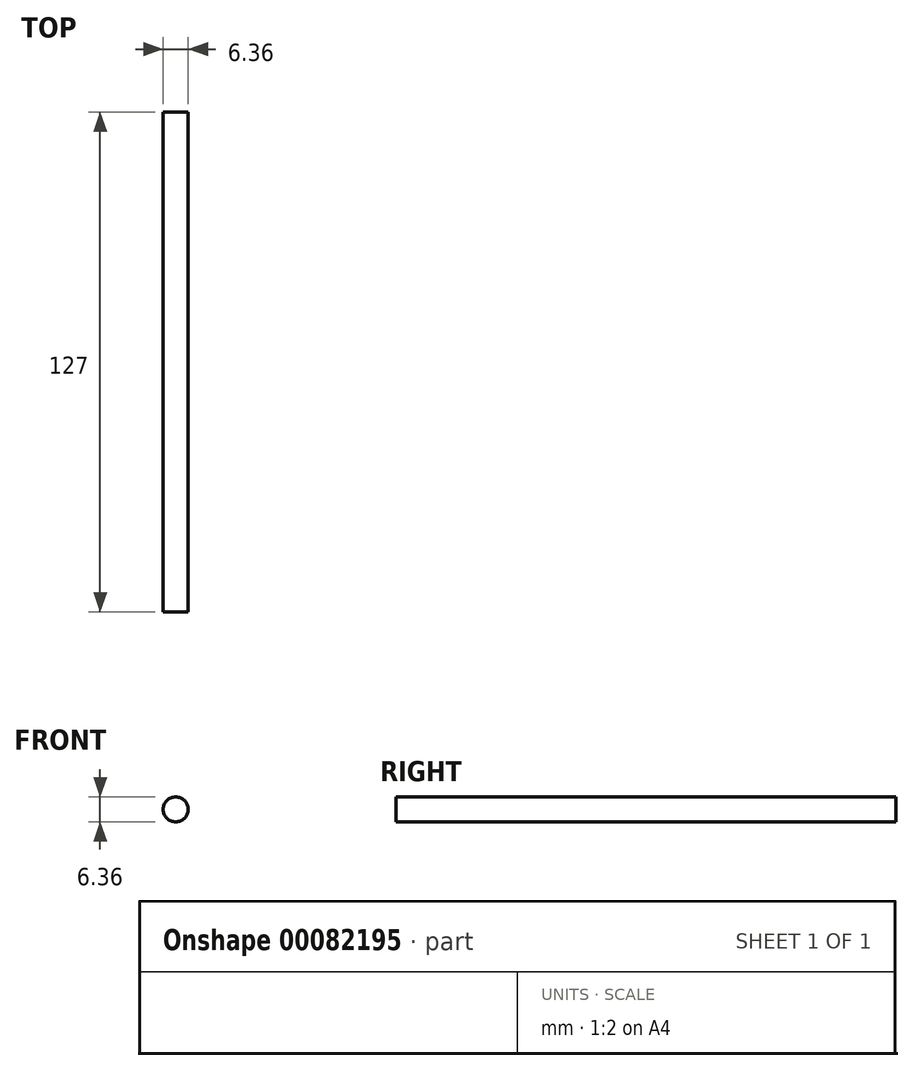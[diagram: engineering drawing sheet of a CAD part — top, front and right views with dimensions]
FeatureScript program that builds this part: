
annotation { "Feature Type Name" : "Feature", "Feature Type Description" : "" }
export const myFeature = defineFeature(function(context is Context, id is Id, definition is map)
    precondition{}
    {
        {
            var Q0;
            Q0=qCreatedBy(makeId("Front.planeOp"),FACE);
            var sketch = newSketch(context, id + "F0", { "sketchPlane" : qUnion([Q0])});
            skCircle(sketch, "E0", {"center": v(0, 0) * mm, "radius": 3.18 * mm});
            skSolve(sketch);
        }
        {
            var Q0;
            Q0 = qSketchRegion(id + "F0", true);
            extrude(context, id + "F1", {"entities" : qUnion([Q0]), "depth" : 127 * mm});
        }
    });
